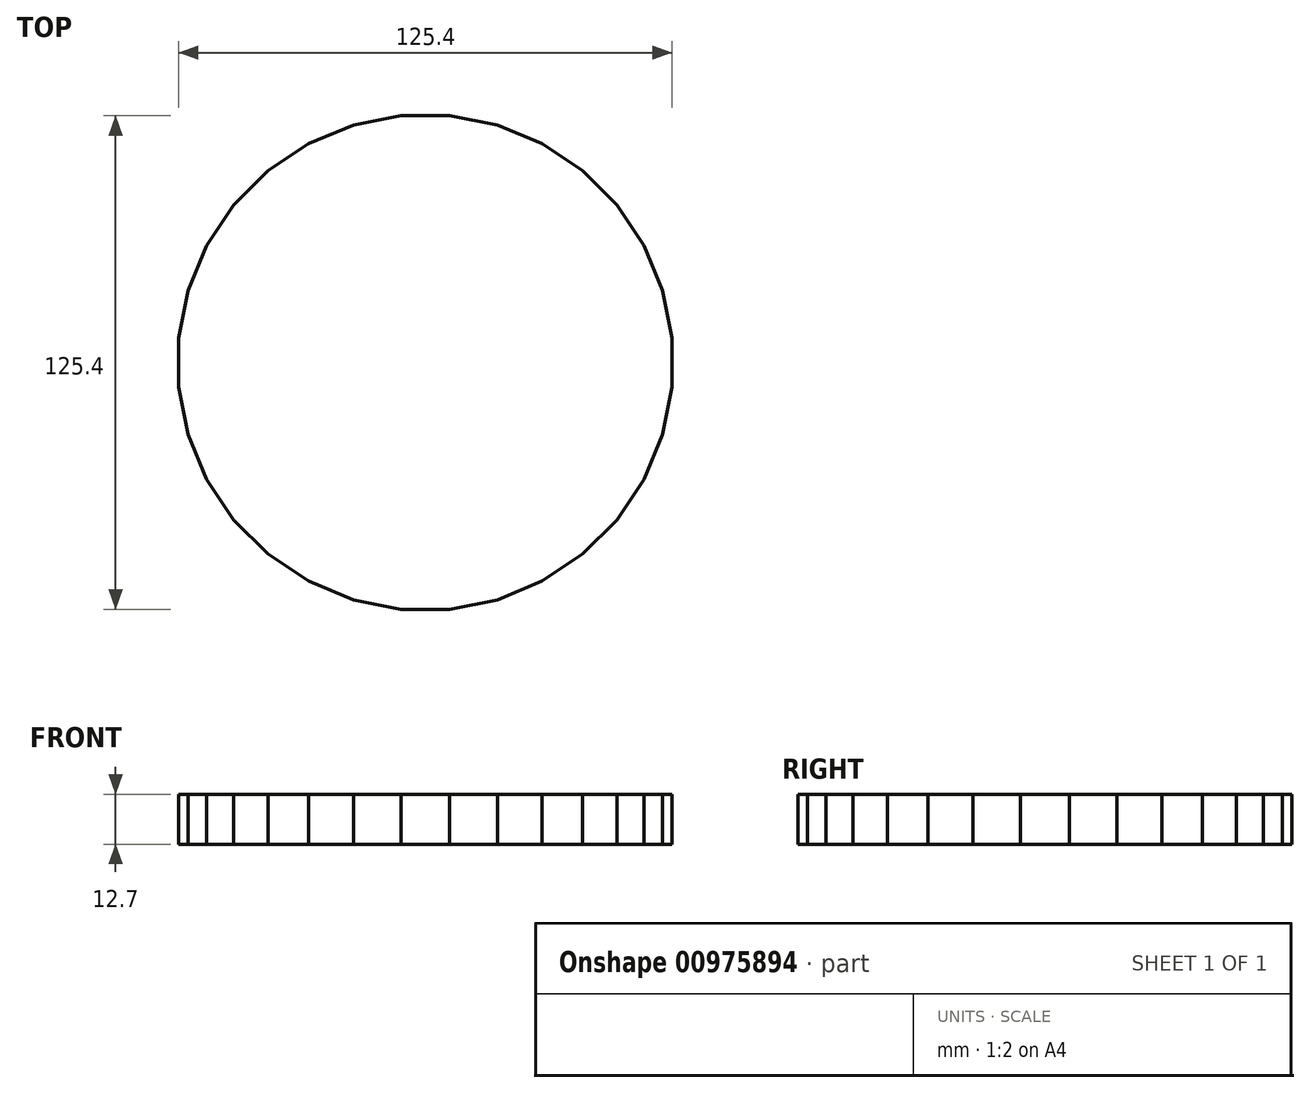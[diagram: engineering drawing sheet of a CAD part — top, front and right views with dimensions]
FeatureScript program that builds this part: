
annotation { "Feature Type Name" : "Feature", "Feature Type Description" : "" }
export const myFeature = defineFeature(function(context is Context, id is Id, definition is map)
    precondition{}
    {
        {
            var Q0;
            Q0=qCreatedBy(makeId("Top.planeOp"),FACE);
            var sketch = newSketch(context, id + "F0", { "sketchPlane" : qUnion([Q0])});
            skCircle(sketch, "E0.cCircle", {"center": v(0, 0) * mm, "radius": 62.7 * mm, "construction": true});
            skLineSegment(sketch, "E0.0", {"start": v(-6.18, 62.7) * mm, "end": v(6.18, 62.7) * mm});
            skLineSegment(sketch, "E0.1", {"start": v(6.18, 62.7) * mm, "end": v(18.29, 60.3) * mm});
            skLineSegment(sketch, "E0.2", {"start": v(18.29, 60.3) * mm, "end": v(29.7, 55.57) * mm});
            skLineSegment(sketch, "E0.3", {"start": v(29.7, 55.57) * mm, "end": v(39.97, 48.7) * mm});
            skLineSegment(sketch, "E0.4", {"start": v(39.97, 48.7) * mm, "end": v(48.7, 39.97) * mm});
            skLineSegment(sketch, "E0.5", {"start": v(48.7, 39.97) * mm, "end": v(55.57, 29.7) * mm});
            skLineSegment(sketch, "E0.6", {"start": v(55.57, 29.7) * mm, "end": v(60.3, 18.29) * mm});
            skLineSegment(sketch, "E0.7", {"start": v(60.3, 18.29) * mm, "end": v(62.7, 6.18) * mm});
            skLineSegment(sketch, "E0.8", {"start": v(62.7, 6.18) * mm, "end": v(62.7, -6.18) * mm});
            skLineSegment(sketch, "E0.9", {"start": v(62.7, -6.18) * mm, "end": v(60.3, -18.29) * mm});
            skLineSegment(sketch, "E0.10", {"start": v(60.3, -18.29) * mm, "end": v(55.57, -29.7) * mm});
            skLineSegment(sketch, "E0.11", {"start": v(55.57, -29.7) * mm, "end": v(48.7, -39.97) * mm});
            skLineSegment(sketch, "E0.12", {"start": v(48.7, -39.97) * mm, "end": v(39.97, -48.7) * mm});
            skLineSegment(sketch, "E0.13", {"start": v(39.97, -48.7) * mm, "end": v(29.7, -55.57) * mm});
            skLineSegment(sketch, "E0.14", {"start": v(29.7, -55.57) * mm, "end": v(18.29, -60.3) * mm});
            skLineSegment(sketch, "E0.15", {"start": v(18.29, -60.3) * mm, "end": v(6.18, -62.7) * mm});
            skLineSegment(sketch, "E0.16", {"start": v(6.18, -62.7) * mm, "end": v(-6.18, -62.7) * mm});
            skLineSegment(sketch, "E0.17", {"start": v(-6.18, -62.7) * mm, "end": v(-18.29, -60.3) * mm});
            skLineSegment(sketch, "E0.18", {"start": v(-18.29, -60.3) * mm, "end": v(-29.7, -55.57) * mm});
            skLineSegment(sketch, "E0.19", {"start": v(-29.7, -55.57) * mm, "end": v(-39.97, -48.7) * mm});
            skLineSegment(sketch, "E0.20", {"start": v(-39.97, -48.7) * mm, "end": v(-48.7, -39.97) * mm});
            skLineSegment(sketch, "E0.21", {"start": v(-48.7, -39.97) * mm, "end": v(-55.57, -29.7) * mm});
            skLineSegment(sketch, "E0.22", {"start": v(-55.57, -29.7) * mm, "end": v(-60.3, -18.29) * mm});
            skLineSegment(sketch, "E0.23", {"start": v(-60.3, -18.29) * mm, "end": v(-62.7, -6.18) * mm});
            skLineSegment(sketch, "E0.24", {"start": v(-62.7, -6.18) * mm, "end": v(-62.7, 6.18) * mm});
            skLineSegment(sketch, "E0.25", {"start": v(-62.7, 6.18) * mm, "end": v(-60.3, 18.29) * mm});
            skLineSegment(sketch, "E0.26", {"start": v(-60.3, 18.29) * mm, "end": v(-55.57, 29.7) * mm});
            skLineSegment(sketch, "E0.27", {"start": v(-55.57, 29.7) * mm, "end": v(-48.7, 39.97) * mm});
            skLineSegment(sketch, "E0.28", {"start": v(-48.7, 39.97) * mm, "end": v(-39.97, 48.7) * mm});
            skLineSegment(sketch, "E0.29", {"start": v(-39.97, 48.7) * mm, "end": v(-29.7, 55.57) * mm});
            skLineSegment(sketch, "E0.30", {"start": v(-29.7, 55.57) * mm, "end": v(-18.29, 60.3) * mm});
            skLineSegment(sketch, "E0.31", {"start": v(-18.29, 60.3) * mm, "end": v(-6.18, 62.7) * mm});
            skPoint(sketch, "E0.0.midPoint", {"position": v(0, 62.7) * mm});
            skCircle(sketch, "E1.cCircle", {"center": v(0, 0) * mm, "radius": 57.8 * mm, "construction": true});
            skLineSegment(sketch, "E1.0", {"start": v(-5.7, 57.8) * mm, "end": v(5.7, 57.8) * mm});
            skLineSegment(sketch, "E1.1", {"start": v(5.7, 57.8) * mm, "end": v(16.86, 55.57) * mm});
            skLineSegment(sketch, "E1.2", {"start": v(16.86, 55.57) * mm, "end": v(27.37, 51.21) * mm});
            skLineSegment(sketch, "E1.3", {"start": v(27.37, 51.21) * mm, "end": v(36.84, 44.9) * mm});
            skLineSegment(sketch, "E1.4", {"start": v(36.84, 44.9) * mm, "end": v(44.9, 36.84) * mm});
            skLineSegment(sketch, "E1.5", {"start": v(44.9, 36.84) * mm, "end": v(51.21, 27.37) * mm});
            skLineSegment(sketch, "E1.6", {"start": v(51.21, 27.37) * mm, "end": v(55.57, 16.86) * mm});
            skLineSegment(sketch, "E1.7", {"start": v(55.57, 16.86) * mm, "end": v(57.8, 5.7) * mm});
            skLineSegment(sketch, "E1.8", {"start": v(57.8, 5.7) * mm, "end": v(57.8, -5.7) * mm});
            skLineSegment(sketch, "E1.9", {"start": v(57.8, -5.7) * mm, "end": v(55.57, -16.86) * mm});
            skLineSegment(sketch, "E1.10", {"start": v(55.57, -16.86) * mm, "end": v(51.21, -27.37) * mm});
            skLineSegment(sketch, "E1.11", {"start": v(51.21, -27.37) * mm, "end": v(44.9, -36.84) * mm});
            skLineSegment(sketch, "E1.12", {"start": v(44.9, -36.84) * mm, "end": v(36.84, -44.9) * mm});
            skLineSegment(sketch, "E1.13", {"start": v(36.84, -44.9) * mm, "end": v(27.37, -51.21) * mm});
            skLineSegment(sketch, "E1.14", {"start": v(27.37, -51.21) * mm, "end": v(16.86, -55.57) * mm});
            skLineSegment(sketch, "E1.15", {"start": v(16.86, -55.57) * mm, "end": v(5.7, -57.8) * mm});
            skLineSegment(sketch, "E1.16", {"start": v(5.7, -57.8) * mm, "end": v(-5.7, -57.8) * mm});
            skLineSegment(sketch, "E1.17", {"start": v(-5.7, -57.8) * mm, "end": v(-16.86, -55.57) * mm});
            skLineSegment(sketch, "E1.18", {"start": v(-16.86, -55.57) * mm, "end": v(-27.37, -51.21) * mm});
            skLineSegment(sketch, "E1.19", {"start": v(-27.37, -51.21) * mm, "end": v(-36.84, -44.9) * mm});
            skLineSegment(sketch, "E1.20", {"start": v(-36.84, -44.9) * mm, "end": v(-44.9, -36.84) * mm});
            skLineSegment(sketch, "E1.21", {"start": v(-44.9, -36.84) * mm, "end": v(-51.21, -27.37) * mm});
            skLineSegment(sketch, "E1.22", {"start": v(-51.21, -27.37) * mm, "end": v(-55.57, -16.86) * mm});
            skLineSegment(sketch, "E1.23", {"start": v(-55.57, -16.86) * mm, "end": v(-57.8, -5.7) * mm});
            skLineSegment(sketch, "E1.24", {"start": v(-57.8, -5.7) * mm, "end": v(-57.8, 5.7) * mm});
            skLineSegment(sketch, "E1.25", {"start": v(-57.8, 5.7) * mm, "end": v(-55.57, 16.86) * mm});
            skLineSegment(sketch, "E1.26", {"start": v(-55.57, 16.86) * mm, "end": v(-51.21, 27.37) * mm});
            skLineSegment(sketch, "E1.27", {"start": v(-51.21, 27.37) * mm, "end": v(-44.9, 36.84) * mm});
            skLineSegment(sketch, "E1.28", {"start": v(-44.9, 36.84) * mm, "end": v(-36.84, 44.9) * mm});
            skLineSegment(sketch, "E1.29", {"start": v(-36.84, 44.9) * mm, "end": v(-27.37, 51.21) * mm});
            skLineSegment(sketch, "E1.30", {"start": v(-27.37, 51.21) * mm, "end": v(-16.86, 55.57) * mm});
            skLineSegment(sketch, "E1.31", {"start": v(-16.86, 55.57) * mm, "end": v(-5.7, 57.8) * mm});
            skPoint(sketch, "E1.0.midPoint", {"position": v(0, 57.8) * mm});
            skLineSegment(sketch, "E2", {"start": v(-39.97, 48.7) * mm, "end": v(-36.84, 44.9) * mm});
            skLineSegment(sketch, "E3", {"start": v(-27.37, 51.21) * mm, "end": v(-29.7, 55.57) * mm});
            skLineSegment(sketch, "E4", {"start": v(-18.29, 60.3) * mm, "end": v(-16.86, 55.57) * mm});
            skLineSegment(sketch, "E5", {"start": v(-5.7, 57.8) * mm, "end": v(-6.18, 62.7) * mm});
            skLineSegment(sketch, "E6", {"start": v(5.7, 57.8) * mm, "end": v(6.18, 62.7) * mm});
            skLineSegment(sketch, "E7", {"start": v(16.86, 55.57) * mm, "end": v(18.29, 60.3) * mm});
            skLineSegment(sketch, "E8", {"start": v(27.37, 51.21) * mm, "end": v(29.7, 55.57) * mm});
            skLineSegment(sketch, "E9", {"start": v(36.84, 44.9) * mm, "end": v(39.97, 48.7) * mm});
            skLineSegment(sketch, "E10", {"start": v(44.9, 36.84) * mm, "end": v(48.7, 39.97) * mm});
            skLineSegment(sketch, "E11", {"start": v(51.21, 27.37) * mm, "end": v(55.57, 29.7) * mm});
            skLineSegment(sketch, "E12", {"start": v(-44.9, 36.84) * mm, "end": v(-48.7, 39.97) * mm});
            skLineSegment(sketch, "E13", {"start": v(-55.57, 29.7) * mm, "end": v(-51.21, 27.37) * mm});
            skLineSegment(sketch, "E14", {"start": v(-55.57, 16.86) * mm, "end": v(-60.3, 18.29) * mm});
            skLineSegment(sketch, "E15", {"start": v(-62.7, 6.18) * mm, "end": v(-57.8, 5.7) * mm});
            skLineSegment(sketch, "E16", {"start": v(-57.8, -5.7) * mm, "end": v(-62.7, -6.18) * mm});
            skLineSegment(sketch, "E17", {"start": v(-55.57, -16.86) * mm, "end": v(-60.3, -18.29) * mm});
            skLineSegment(sketch, "E18", {"start": v(-51.21, -27.37) * mm, "end": v(-55.57, -29.7) * mm});
            skLineSegment(sketch, "E19", {"start": v(-48.7, -39.97) * mm, "end": v(-44.9, -36.84) * mm});
            skLineSegment(sketch, "E20", {"start": v(-39.97, -48.7) * mm, "end": v(-36.84, -44.9) * mm});
            skLineSegment(sketch, "E21", {"start": v(-29.7, -55.57) * mm, "end": v(-27.37, -51.21) * mm});
            skLineSegment(sketch, "E22", {"start": v(-18.29, -60.3) * mm, "end": v(-16.86, -55.57) * mm});
            skLineSegment(sketch, "E23", {"start": v(-6.18, -62.7) * mm, "end": v(-5.7, -57.8) * mm});
            skLineSegment(sketch, "E24", {"start": v(29.7, -55.57) * mm, "end": v(27.37, -51.21) * mm});
            skLineSegment(sketch, "E25", {"start": v(16.86, -55.57) * mm, "end": v(18.29, -60.3) * mm});
            skLineSegment(sketch, "E26", {"start": v(5.7, -57.8) * mm, "end": v(6.18, -62.7) * mm});
            skLineSegment(sketch, "E27", {"start": v(36.84, -44.9) * mm, "end": v(39.97, -48.7) * mm});
            skLineSegment(sketch, "E28", {"start": v(44.9, -36.84) * mm, "end": v(48.7, -39.97) * mm});
            skLineSegment(sketch, "E29", {"start": v(51.21, -27.37) * mm, "end": v(55.57, -29.7) * mm});
            skLineSegment(sketch, "E30", {"start": v(55.57, -16.86) * mm, "end": v(60.3, -18.29) * mm});
            skLineSegment(sketch, "E31", {"start": v(60.3, 18.29) * mm, "end": v(55.57, 16.86) * mm});
            skLineSegment(sketch, "E32", {"start": v(57.8, 5.7) * mm, "end": v(62.7, 6.18) * mm});
            skLineSegment(sketch, "E33", {"start": v(57.8, -5.7) * mm, "end": v(62.7, -6.18) * mm});
            skSolve(sketch);
        }
        {
            var Q0;
            Q0=makeQuery(id+"F0.imprint","IMPRINT",FACE,{"disambiguationData":[TD([[makeQuery(id+"F0.imprint","IMPRINT",EDGE,{"derivedFrom":sQuery(id+"F0.wireOp",EDGE,"E0.15")}),-1.0]])]});
            var Q1;
            Q1=makeQuery(id+"F0.imprint","IMPRINT",FACE,{"disambiguationData":[TD([[makeQuery(id+"F0.imprint","IMPRINT",EDGE,{"derivedFrom":sQuery(id+"F0.wireOp",EDGE,"E0.20")}),-1.0]])]});
            var Q2;
            Q2=makeQuery(id+"F0.imprint","IMPRINT",FACE,{"disambiguationData":[TD([[makeQuery(id+"F0.imprint","IMPRINT",EDGE,{"derivedFrom":sQuery(id+"F0.wireOp",EDGE,"E0.22")}),-1.0]])]});
            var Q3;
            Q3=makeQuery(id+"F0.imprint","IMPRINT",FACE,{"disambiguationData":[TD([[makeQuery(id+"F0.imprint","IMPRINT",EDGE,{"derivedFrom":sQuery(id+"F0.wireOp",EDGE,"E1.0")}),-1.0]])]});
            var Q4;
            Q4=makeQuery(id+"F0.imprint","IMPRINT",FACE,{"disambiguationData":[TD([[makeQuery(id+"F0.imprint","IMPRINT",EDGE,{"derivedFrom":sQuery(id+"F0.wireOp",EDGE,"E0.8")}),-1.0]])]});
            var Q5;
            Q5=makeQuery(id+"F0.imprint","IMPRINT",FACE,{"disambiguationData":[TD([[makeQuery(id+"F0.imprint","IMPRINT",EDGE,{"derivedFrom":sQuery(id+"F0.wireOp",EDGE,"E0.9")}),-1.0]])]});
            var Q6;
            Q6=makeQuery(id+"F0.imprint","IMPRINT",FACE,{"disambiguationData":[TD([[makeQuery(id+"F0.imprint","IMPRINT",EDGE,{"derivedFrom":sQuery(id+"F0.wireOp",EDGE,"E0.18")}),-1.0]])]});
            var Q7;
            Q7=makeQuery(id+"F0.imprint","IMPRINT",FACE,{"disambiguationData":[TD([[makeQuery(id+"F0.imprint","IMPRINT",EDGE,{"derivedFrom":sQuery(id+"F0.wireOp",EDGE,"E0.10")}),-1.0]])]});
            var Q8;
            Q8=makeQuery(id+"F0.imprint","IMPRINT",FACE,{"disambiguationData":[TD([[makeQuery(id+"F0.imprint","IMPRINT",EDGE,{"derivedFrom":sQuery(id+"F0.wireOp",EDGE,"E0.1")}),-1.0]])]});
            var Q9;
            Q9=makeQuery(id+"F0.imprint","IMPRINT",FACE,{"disambiguationData":[TD([[makeQuery(id+"F0.imprint","IMPRINT",EDGE,{"derivedFrom":sQuery(id+"F0.wireOp",EDGE,"E0.2")}),-1.0]])]});
            var Q10;
            Q10=makeQuery(id+"F0.imprint","IMPRINT",FACE,{"disambiguationData":[TD([[makeQuery(id+"F0.imprint","IMPRINT",EDGE,{"derivedFrom":sQuery(id+"F0.wireOp",EDGE,"E0.24")}),-1.0]])]});
            var Q11;
            Q11=makeQuery(id+"F0.imprint","IMPRINT",FACE,{"disambiguationData":[TD([[makeQuery(id+"F0.imprint","IMPRINT",EDGE,{"derivedFrom":sQuery(id+"F0.wireOp",EDGE,"E0.23")}),-1.0]])]});
            var Q12;
            Q12=makeQuery(id+"F0.imprint","IMPRINT",FACE,{"disambiguationData":[TD([[makeQuery(id+"F0.imprint","IMPRINT",EDGE,{"derivedFrom":sQuery(id+"F0.wireOp",EDGE,"E0.28")}),-1.0]])]});
            var Q13;
            Q13=makeQuery(id+"F0.imprint","IMPRINT",FACE,{"disambiguationData":[TD([[makeQuery(id+"F0.imprint","IMPRINT",EDGE,{"derivedFrom":sQuery(id+"F0.wireOp",EDGE,"E0.29")}),-1.0]])]});
            var Q14;
            Q14=makeQuery(id+"F0.imprint","IMPRINT",FACE,{"disambiguationData":[TD([[makeQuery(id+"F0.imprint","IMPRINT",EDGE,{"derivedFrom":sQuery(id+"F0.wireOp",EDGE,"E0.4")}),-1.0]])]});
            var Q15;
            Q15=makeQuery(id+"F0.imprint","IMPRINT",FACE,{"disambiguationData":[TD([[makeQuery(id+"F0.imprint","IMPRINT",EDGE,{"derivedFrom":sQuery(id+"F0.wireOp",EDGE,"E0.30")}),-1.0]])]});
            var Q16;
            Q16=makeQuery(id+"F0.imprint","IMPRINT",FACE,{"disambiguationData":[TD([[makeQuery(id+"F0.imprint","IMPRINT",EDGE,{"derivedFrom":sQuery(id+"F0.wireOp",EDGE,"E0.19")}),-1.0]])]});
            var Q17;
            Q17=makeQuery(id+"F0.imprint","IMPRINT",FACE,{"disambiguationData":[TD([[makeQuery(id+"F0.imprint","IMPRINT",EDGE,{"derivedFrom":sQuery(id+"F0.wireOp",EDGE,"E0.3")}),-1.0]])]});
            var Q18;
            Q18=makeQuery(id+"F0.imprint","IMPRINT",FACE,{"disambiguationData":[TD([[makeQuery(id+"F0.imprint","IMPRINT",EDGE,{"derivedFrom":sQuery(id+"F0.wireOp",EDGE,"E0.13")}),-1.0]])]});
            var Q19;
            Q19=makeQuery(id+"F0.imprint","IMPRINT",FACE,{"disambiguationData":[TD([[makeQuery(id+"F0.imprint","IMPRINT",EDGE,{"derivedFrom":sQuery(id+"F0.wireOp",EDGE,"E0.21")}),-1.0]])]});
            var Q20;
            Q20=makeQuery(id+"F0.imprint","IMPRINT",FACE,{"disambiguationData":[TD([[makeQuery(id+"F0.imprint","IMPRINT",EDGE,{"derivedFrom":sQuery(id+"F0.wireOp",EDGE,"E0.16")}),-1.0]])]});
            var Q21;
            Q21=makeQuery(id+"F0.imprint","IMPRINT",FACE,{"disambiguationData":[TD([[makeQuery(id+"F0.imprint","IMPRINT",EDGE,{"derivedFrom":sQuery(id+"F0.wireOp",EDGE,"E0.11")}),-1.0]])]});
            var Q22;
            Q22=makeQuery(id+"F0.imprint","IMPRINT",FACE,{"disambiguationData":[TD([[makeQuery(id+"F0.imprint","IMPRINT",EDGE,{"derivedFrom":sQuery(id+"F0.wireOp",EDGE,"E0.14")}),-1.0]])]});
            var Q23;
            Q23=makeQuery(id+"F0.imprint","IMPRINT",FACE,{"disambiguationData":[TD([[makeQuery(id+"F0.imprint","IMPRINT",EDGE,{"derivedFrom":sQuery(id+"F0.wireOp",EDGE,"E0.12")}),-1.0]])]});
            var Q24;
            Q24=makeQuery(id+"F0.imprint","IMPRINT",FACE,{"disambiguationData":[TD([[makeQuery(id+"F0.imprint","IMPRINT",EDGE,{"derivedFrom":sQuery(id+"F0.wireOp",EDGE,"E0.0")}),-1.0]])]});
            var Q25;
            Q25=makeQuery(id+"F0.imprint","IMPRINT",FACE,{"disambiguationData":[TD([[makeQuery(id+"F0.imprint","IMPRINT",EDGE,{"derivedFrom":sQuery(id+"F0.wireOp",EDGE,"E0.26")}),-1.0]])]});
            var Q26;
            Q26=makeQuery(id+"F0.imprint","IMPRINT",FACE,{"disambiguationData":[TD([[makeQuery(id+"F0.imprint","IMPRINT",EDGE,{"derivedFrom":sQuery(id+"F0.wireOp",EDGE,"E0.5")}),-1.0]])]});
            var Q27;
            Q27=makeQuery(id+"F0.imprint","IMPRINT",FACE,{"disambiguationData":[TD([[makeQuery(id+"F0.imprint","IMPRINT",EDGE,{"derivedFrom":sQuery(id+"F0.wireOp",EDGE,"E0.31")}),-1.0]])]});
            var Q28;
            Q28=makeQuery(id+"F0.imprint","IMPRINT",FACE,{"disambiguationData":[TD([[makeQuery(id+"F0.imprint","IMPRINT",EDGE,{"derivedFrom":sQuery(id+"F0.wireOp",EDGE,"E0.25")}),-1.0]])]});
            var Q29;
            Q29=makeQuery(id+"F0.imprint","IMPRINT",FACE,{"disambiguationData":[TD([[makeQuery(id+"F0.imprint","IMPRINT",EDGE,{"derivedFrom":sQuery(id+"F0.wireOp",EDGE,"E0.6")}),-1.0]])]});
            var Q30;
            Q30=makeQuery(id+"F0.imprint","IMPRINT",FACE,{"disambiguationData":[TD([[makeQuery(id+"F0.imprint","IMPRINT",EDGE,{"derivedFrom":sQuery(id+"F0.wireOp",EDGE,"E0.7")}),-1.0]])]});
            var Q31;
            Q31=makeQuery(id+"F0.imprint","IMPRINT",FACE,{"disambiguationData":[TD([[makeQuery(id+"F0.imprint","IMPRINT",EDGE,{"derivedFrom":sQuery(id+"F0.wireOp",EDGE,"E0.27")}),-1.0]])]});
            var Q32;
            Q32=makeQuery(id+"F0.imprint","IMPRINT",FACE,{"disambiguationData":[TD([[makeQuery(id+"F0.imprint","IMPRINT",EDGE,{"derivedFrom":sQuery(id+"F0.wireOp",EDGE,"E0.17")}),-1.0]])]});
            extrude(context, id + "F1", {"entities" : qUnion([Q0, Q1, Q2, Q3, Q4, Q5, Q6, Q7, Q8, Q9, Q10, Q11, Q12, Q13, Q14, Q15, Q16, Q17, Q18, Q19, Q20, Q21, Q22, Q23, Q24, Q25, Q26, Q27, Q28, Q29, Q30, Q31, Q32]), "depth" : 12.7 * mm, "offsetDistance" : 25.4 * mm});
        }
    });
